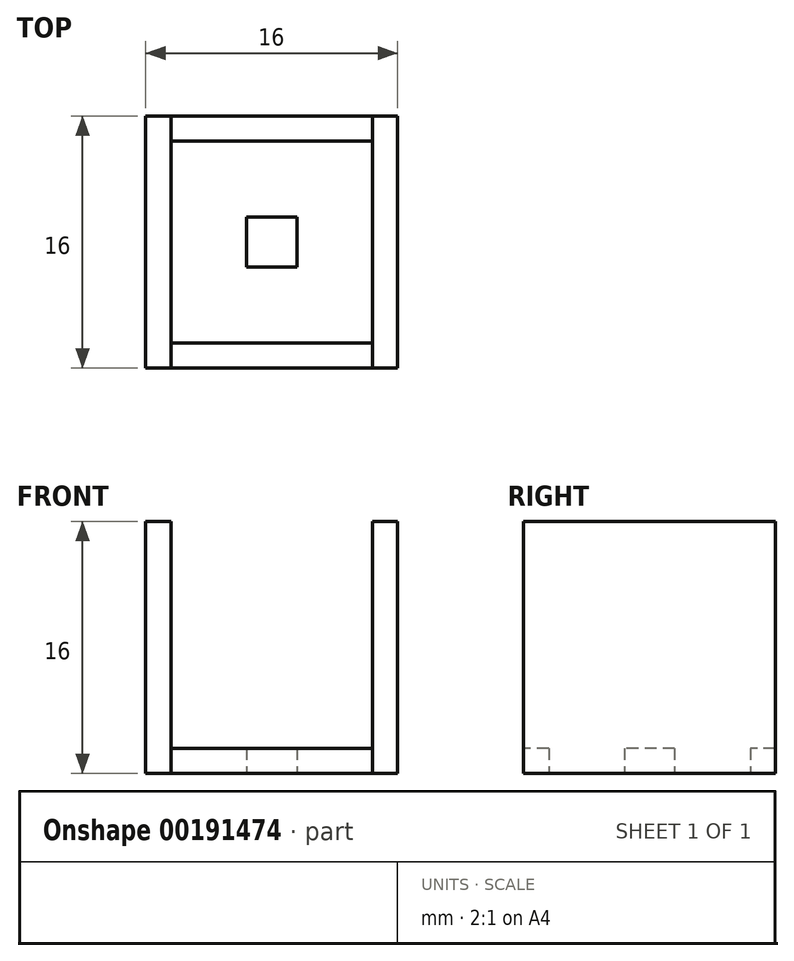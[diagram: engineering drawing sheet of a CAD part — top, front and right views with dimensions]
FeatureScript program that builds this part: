
annotation { "Feature Type Name" : "Feature", "Feature Type Description" : "" }
export const myFeature = defineFeature(function(context is Context, id is Id, definition is map)
    precondition{}
    {
        {
            assignVariable(context, id + "F0", {"name" : "FLU", "anyValue" : 1.6});
        }
        {
            var Q0;
            Q0=qCreatedBy(makeId("Top.planeOp"),FACE);
            var sketch = newSketch(context, id + "F1", { "sketchPlane" : qUnion([Q0])});
            skLineSegment(sketch, "E0.bottom", {"start": v(8, 8) * mm, "end": v(-8, 8) * mm});
            skLineSegment(sketch, "E0.top", {"start": v(8, -8) * mm, "end": v(-8, -8) * mm});
            skLineSegment(sketch, "E0.left", {"start": v(8, 8) * mm, "end": v(8, -8) * mm});
            skLineSegment(sketch, "E0.right", {"start": v(-8, 8) * mm, "end": v(-8, -8) * mm});
            skPoint(sketch, "E0.middle", {"position": v(0, 0) * mm});
            skLineSegment(sketch, "E1", {"start": v(-6.4, 8) * mm, "end": v(-6.4, -8) * mm});
            skLineSegment(sketch, "E2", {"start": v(6.4, 8) * mm, "end": v(6.4, -8) * mm});
            skLineSegment(sketch, "E3", {"start": v(-8, 6.4) * mm, "end": v(8, 6.4) * mm});
            skLineSegment(sketch, "E4", {"start": v(-8, -6.4) * mm, "end": v(8.33, -6.4) * mm});
            skLineSegment(sketch, "E5.bottom", {"start": v(1.6, 6.4) * mm, "end": v(-1.6, 6.4) * mm});
            skLineSegment(sketch, "E5.top", {"start": v(1.6, -6.4) * mm, "end": v(-1.6, -6.4) * mm});
            skLineSegment(sketch, "E5.left", {"start": v(1.6, 6.4) * mm, "end": v(1.6, -6.4) * mm});
            skLineSegment(sketch, "E5.right", {"start": v(-1.6, 6.4) * mm, "end": v(-1.6, -6.4) * mm});
            skLineSegment(sketch, "E6.bottom", {"start": v(6.4, 1.6) * mm, "end": v(-6.4, 1.6) * mm});
            skLineSegment(sketch, "E6.top", {"start": v(6.4, -1.6) * mm, "end": v(-6.4, -1.6) * mm});
            skLineSegment(sketch, "E6.left", {"start": v(6.4, 1.6) * mm, "end": v(6.4, -1.6) * mm});
            skLineSegment(sketch, "E6.right", {"start": v(-6.4, 1.6) * mm, "end": v(-6.4, -1.6) * mm});
            skSolve(sketch);
        }
        {
            var Q0;
            {var subQ0=sQuery(id+"F1.wireOp",EDGE,"E3");var subQ1=sQuery(id+"F1.wireOp",EDGE,"E0.right");var subQ2=makeQuery(id+"F1.imprint","INTERSECT",VERTEX,{"derivedFrom":[subQ1,subQ0]});Q0=makeQuery(id+"F1.imprint","IMPRINT",FACE,{"disambiguationData":[TD([[makeQuery(id+"F1.imprint","IMPRINT",EDGE,{"disambiguationData":[TD([[subQ2,-1.0]])],"derivedFrom":subQ1}),1.0]])]});}
            var Q1;
            {var subQ0=sQuery(id+"F1.wireOp",EDGE,"E0.right");var subQ1=sQuery(id+"F1.wireOp",EDGE,"E0.top");var subQ2=makeQuery(id+"F1.imprint","INTERSECT",VERTEX,{"derivedFrom":[subQ1,subQ0]});Q1=makeQuery(id+"F1.imprint","IMPRINT",FACE,{"disambiguationData":[TD([[makeQuery(id+"F1.imprint","IMPRINT",EDGE,{"disambiguationData":[TD([[subQ2,1.0]])],"derivedFrom":subQ1}),-1.0]])]});}
            var Q2;
            {var subQ0=sQuery(id+"F1.wireOp",EDGE,"E0.right");var subQ1=sQuery(id+"F1.wireOp",EDGE,"E0.bottom");var subQ2=makeQuery(id+"F1.imprint","INTERSECT",VERTEX,{"derivedFrom":[subQ1,subQ0]});Q2=makeQuery(id+"F1.imprint","IMPRINT",FACE,{"disambiguationData":[TD([[makeQuery(id+"F1.imprint","IMPRINT",EDGE,{"disambiguationData":[TD([[subQ2,1.0]])],"derivedFrom":subQ1}),1.0]])]});}
            var Q3;
            {var subQ0=sQuery(id+"F1.wireOp",EDGE,"E0.left");var subQ1=sQuery(id+"F1.wireOp",EDGE,"E0.bottom");var subQ2=makeQuery(id+"F1.imprint","INTERSECT",VERTEX,{"derivedFrom":[subQ1,subQ0]});Q3=makeQuery(id+"F1.imprint","IMPRINT",FACE,{"disambiguationData":[TD([[makeQuery(id+"F1.imprint","IMPRINT",EDGE,{"disambiguationData":[TD([[subQ2,-1.0]])],"derivedFrom":subQ1}),1.0]])]});}
            var Q4;
            {var subQ0=sQuery(id+"F1.wireOp",EDGE,"E3");var subQ1=sQuery(id+"F1.wireOp",EDGE,"E0.left");var subQ2=makeQuery(id+"F1.imprint","INTERSECT",VERTEX,{"derivedFrom":[subQ1,subQ0]});Q4=makeQuery(id+"F1.imprint","IMPRINT",FACE,{"disambiguationData":[TD([[makeQuery(id+"F1.imprint","IMPRINT",EDGE,{"disambiguationData":[TD([[subQ2,-1.0]])],"derivedFrom":subQ1}),-1.0]])]});}
            var Q5;
            {var subQ0=sQuery(id+"F1.wireOp",EDGE,"E0.left");var subQ1=sQuery(id+"F1.wireOp",EDGE,"E0.top");var subQ2=makeQuery(id+"F1.imprint","INTERSECT",VERTEX,{"derivedFrom":[subQ1,subQ0]});Q5=makeQuery(id+"F1.imprint","IMPRINT",FACE,{"disambiguationData":[TD([[makeQuery(id+"F1.imprint","IMPRINT",EDGE,{"disambiguationData":[TD([[subQ2,-1.0]])],"derivedFrom":subQ1}),-1.0]])]});}
            extrude(context, id + "F2", {"entities" : qUnion([Q0, Q1, Q2, Q3, Q4, Q5]), "depth" : (10 * getVariable(context, 'FLU')) * mm});
        }
        {
            var Q0;
            {var subQ0=sQuery(id+"F1.wireOp",EDGE,"E1");var subQ1=sQuery(id+"F1.wireOp",EDGE,"E0.bottom");var subQ2=makeQuery(id+"F1.imprint","INTERSECT",VERTEX,{"derivedFrom":[subQ1,subQ0]});Q0=makeQuery(id+"F1.imprint","IMPRINT",FACE,{"disambiguationData":[TD([[makeQuery(id+"F1.imprint","IMPRINT",EDGE,{"disambiguationData":[TD([[subQ2,1.0]])],"derivedFrom":subQ1}),1.0]])]});}
            var Q1;
            {var subQ0=sQuery(id+"F1.wireOp",EDGE,"E1");var subQ1=sQuery(id+"F1.wireOp",EDGE,"E0.top");var subQ2=makeQuery(id+"F1.imprint","INTERSECT",VERTEX,{"derivedFrom":[subQ1,subQ0]});Q1=makeQuery(id+"F1.imprint","IMPRINT",FACE,{"disambiguationData":[TD([[makeQuery(id+"F1.imprint","IMPRINT",EDGE,{"disambiguationData":[TD([[subQ2,1.0]])],"derivedFrom":subQ1}),-1.0]])]});}
            var Q2;
            {var subQ0=sQuery(id+"F1.wireOp",EDGE,"E5.bottom");Q2=makeQuery(id+"F1.imprint","IMPRINT",FACE,{"disambiguationData":[TD([[makeQuery(id+"F1.imprint","IMPRINT",EDGE,{"derivedFrom":subQ0}),1.0]])]});}
            var Q3;
            {var subQ5=sQuery(id+"F1.wireOp",EDGE,"E6.right");Q3=makeQuery(id+"F1.imprint","IMPRINT",FACE,{"disambiguationData":[TD([[makeQuery(id+"F1.imprint","IMPRINT",EDGE,{"derivedFrom":subQ5}),1.0]])]});}
            var Q4;
            {var subQ0=sQuery(id+"F1.wireOp",EDGE,"E6.bottom");var subQ1=sQuery(id+"F1.wireOp",EDGE,"E5.left");var subQ2=makeQuery(id+"F1.imprint","INTERSECT",VERTEX,{"derivedFrom":[subQ1,subQ0]});Q4=makeQuery(id+"F1.imprint","IMPRINT",FACE,{"disambiguationData":[TD([[makeQuery(id+"F1.imprint","IMPRINT",EDGE,{"disambiguationData":[TD([[subQ2,-1.0]])],"derivedFrom":subQ1}),-1.0]])]});}
            var Q5;
            {var subQ5=sQuery(id+"F1.wireOp",EDGE,"E6.left");Q5=makeQuery(id+"F1.imprint","IMPRINT",FACE,{"disambiguationData":[TD([[makeQuery(id+"F1.imprint","IMPRINT",EDGE,{"derivedFrom":subQ5}),-1.0]])]});}
            var Q6;
            {var subQ0=sQuery(id+"F1.wireOp",EDGE,"E5.top");Q6=makeQuery(id+"F1.imprint","IMPRINT",FACE,{"disambiguationData":[TD([[makeQuery(id+"F1.imprint","IMPRINT",EDGE,{"derivedFrom":subQ0}),-1.0]])]});}
            extrude(context, id + "F3", {"entities" : qUnion([Q0, Q1, Q2, Q3, Q4, Q5, Q6]), "depth" : (getVariable(context, 'FLU')) * mm});
        }
    });
